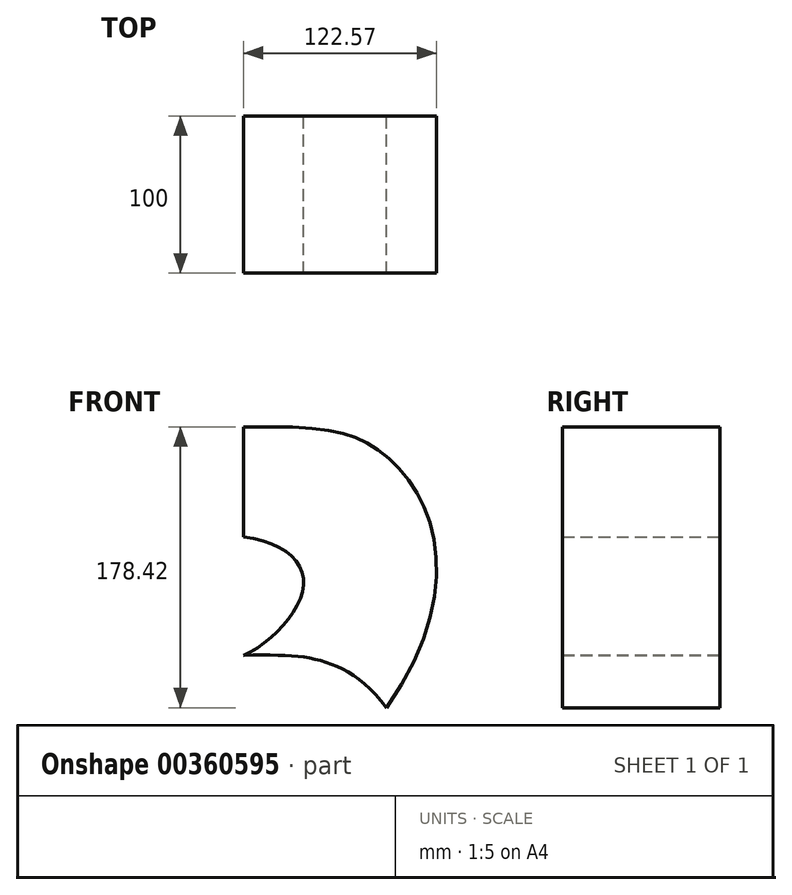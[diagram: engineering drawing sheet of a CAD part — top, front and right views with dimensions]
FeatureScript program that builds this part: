
annotation { "Feature Type Name" : "Feature", "Feature Type Description" : "" }
export const myFeature = defineFeature(function(context is Context, id is Id, definition is map)
    precondition{}
    {
        {
            var Q0;
            Q0=qCreatedBy(makeId("Front.planeOp"),FACE);
            var sketch = newSketch(context, id + "F0", { "sketchPlane" : qUnion([Q0])});
            skLineSegment(sketch, "E0", {"start": v(-40.19, 19.4) * mm, "end": v(-40.19, 89.4) * mm});
            skFitSpline(sketch, "E1", {"points": [v(-40.19, 19.4) * mm, v(-2.04, -10.9) * mm, v(-40.19, -55.6) * mm], "startDerivative": vector(154.58, -15.95) * mm, "endDerivative": vector(-99.47, -43.66) * mm});
            skFitSpline(sketch, "E2", {"points": [v(-40.19, -55.6) * mm, v(10.96, -59.66) * mm, v(50.55, -88.9) * mm], "startDerivative": vector(146.1, 2.51) * mm, "endDerivative": vector(80.79, -106.03) * mm});
            skFitSpline(sketch, "E3", {"points": [v(50.55, -88.9) * mm, v(77.73, 29.94) * mm, v(42.02, 76.95) * mm, v(-40.19, 89.4) * mm], "startDerivative": vector(245.7, 345.16) * mm, "endDerivative": vector(-419.13, -6.2) * mm});
            skLineSegment(sketch, "E4", {"start": v(-58.84, -88.9) * mm, "end": v(132.1, -88.9) * mm, "construction": true});
            skLineSegment(sketch, "E5", {"start": v(82.38, -88.9) * mm, "end": v(82.38, 117.9) * mm, "construction": true});
            skSolve(sketch);
        }
        {
            var Q0;
            Q0 = qSketchRegion(id + "F0", true);
            extrude(context, id + "F1", {"entities" : qUnion([Q0]), "depth" : 100 * mm});
        }
    });
